# Revit family: QF_ MACOM_FP72C
name_source: partatom
category: Equipamento especial
units: mm (PartAtom-declared; Revit-internal decimal feet)

## family parameters
Com base no plano de trabalho = Não
Compartilhado = Não
Corte com vazios quando carregada = Não
Cota do conector redondo = Utilizar diâmetro
Número OmniClass = 23.40.40.14.17.11
Ponto de cálculo do ambiente = Não
Sempre na vertical = Sim
Tipo de parte = Normal
Título OmniClass = Cookers, Ovens, Stoves

## types (2) — shared parameters
Descrição = FOGÃO FRANCES DE ENCOSTO A GÁS 720 MACOM
Elevação padrão = 0,000 mm
Fabricante = MACOM
Gas Connection Height = 72,000 mm
Gas Size = 1"
Height = 245,000 mm
Length = 745,000 mm
Show Logo = Sim
URL = http://www.acosmacom.com.br
Volume = 0,13 m³
Weight = 78,00 kg
Width = 720,000 mm

## per-type parameters (varying)
| type | Gas Consumption GLP | Gas Consumption GN | Gas Input GLP | Gas Input GN | Gas Pressure | Number of Burners |
| FP72C-N |  | 0,79 m³/h | 0 Btu | 7488 Kcal/h | 0,022 bar | 1 |
| FP72C-G | 0,65 Kg/h | 0,00 m³/h | 29712 Btu |  | 0,029 bar | 0 |

note: column(s) folded — value = type name in every type: Modelo

## geometry (parser evidence)
native form markers: Sweep x6
no freeform markers — native parametric forms only
